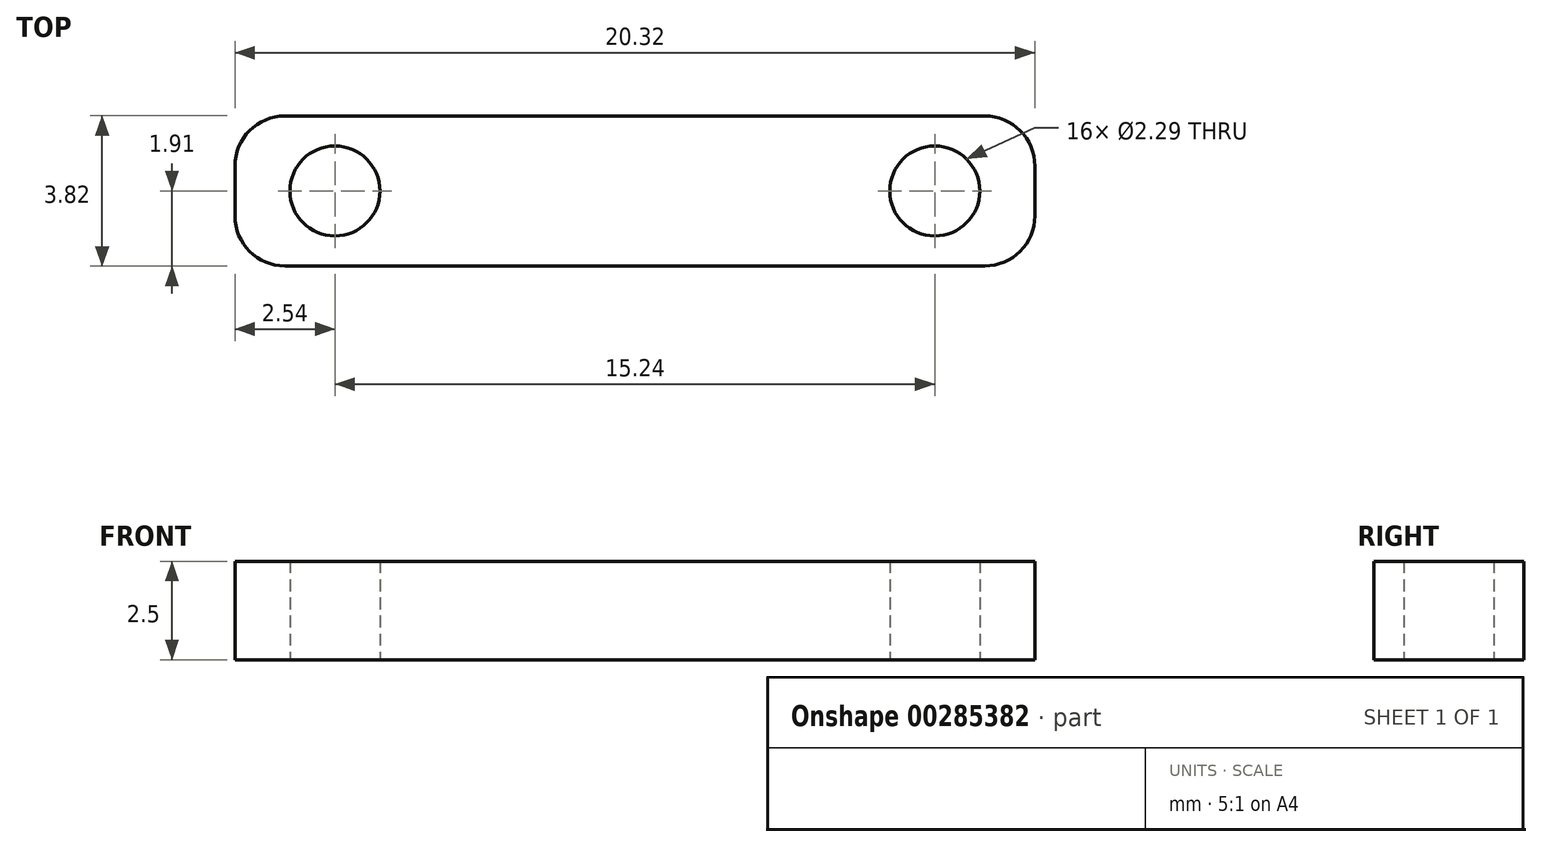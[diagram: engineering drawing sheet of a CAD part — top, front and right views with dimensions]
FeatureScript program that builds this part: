
annotation { "Feature Type Name" : "Feature", "Feature Type Description" : "" }
export const myFeature = defineFeature(function(context is Context, id is Id, definition is map)
    precondition{}
    {
        {
            var Q0;
            Q0=qCreatedBy(makeId("Top.planeOp"),FACE);
            var sketch = newSketch(context, id + "F0", { "sketchPlane" : qUnion([Q0])});
            skLineSegment(sketch, "E0.bottom", {"start": v(-10.16, 1.9) * mm, "end": v(10.16, 1.9) * mm});
            skLineSegment(sketch, "E0.top", {"start": v(-10.16, -1.9) * mm, "end": v(10.16, -1.9) * mm});
            skLineSegment(sketch, "E0.left", {"start": v(-10.16, 1.9) * mm, "end": v(-10.16, -1.9) * mm});
            skLineSegment(sketch, "E0.right", {"start": v(10.16, 1.9) * mm, "end": v(10.16, -1.9) * mm});
            skCircle(sketch, "E1", {"center": v(-7.62, 0) * mm, "radius": 1.14 * mm});
            skCircle(sketch, "E2", {"center": v(7.62, 0) * mm, "radius": 1.14 * mm});
            skSolve(sketch);
        }
        {
            var Q0;
            Q0 = qSketchRegion(id + "F0", true);
            extrude(context, id + "F1", {"entities" : qUnion([Q0]), "depth" : 2.5 * mm});
        }
        {
            var Q0;
            Q0=makeQuery(id+"F1.opExtrude","SWEPT_EDGE",EDGE,{"disambiguationData":[OSD([sQuery(id+"F0.wireOp",EDGE,"E0.bottom"),sQuery(id+"F0.wireOp",EDGE,"E0.right")])]});
            var Q1;
            Q1=makeQuery(id+"F1.opExtrude","SWEPT_EDGE",EDGE,{"disambiguationData":[OSD([sQuery(id+"F0.wireOp",EDGE,"E0.top"),sQuery(id+"F0.wireOp",EDGE,"E0.right")])]});
            var Q2;
            Q2=makeQuery(id+"F1.opExtrude","SWEPT_EDGE",EDGE,{"disambiguationData":[OSD([sQuery(id+"F0.wireOp",EDGE,"E0.bottom"),sQuery(id+"F0.wireOp",EDGE,"E0.left")])]});
            var Q3;
            Q3=makeQuery(id+"F1.opExtrude","SWEPT_EDGE",EDGE,{"disambiguationData":[OSD([sQuery(id+"F0.wireOp",EDGE,"E0.top"),sQuery(id+"F0.wireOp",EDGE,"E0.left")])]});
            fillet(context, id + "F2", {"entities" : qUnion([Q0, Q1, Q2, Q3]), "radius" : 1.27 * mm, "tangentPropagation" : true, "allowEdgeOverflow" : false});
        }
    });
